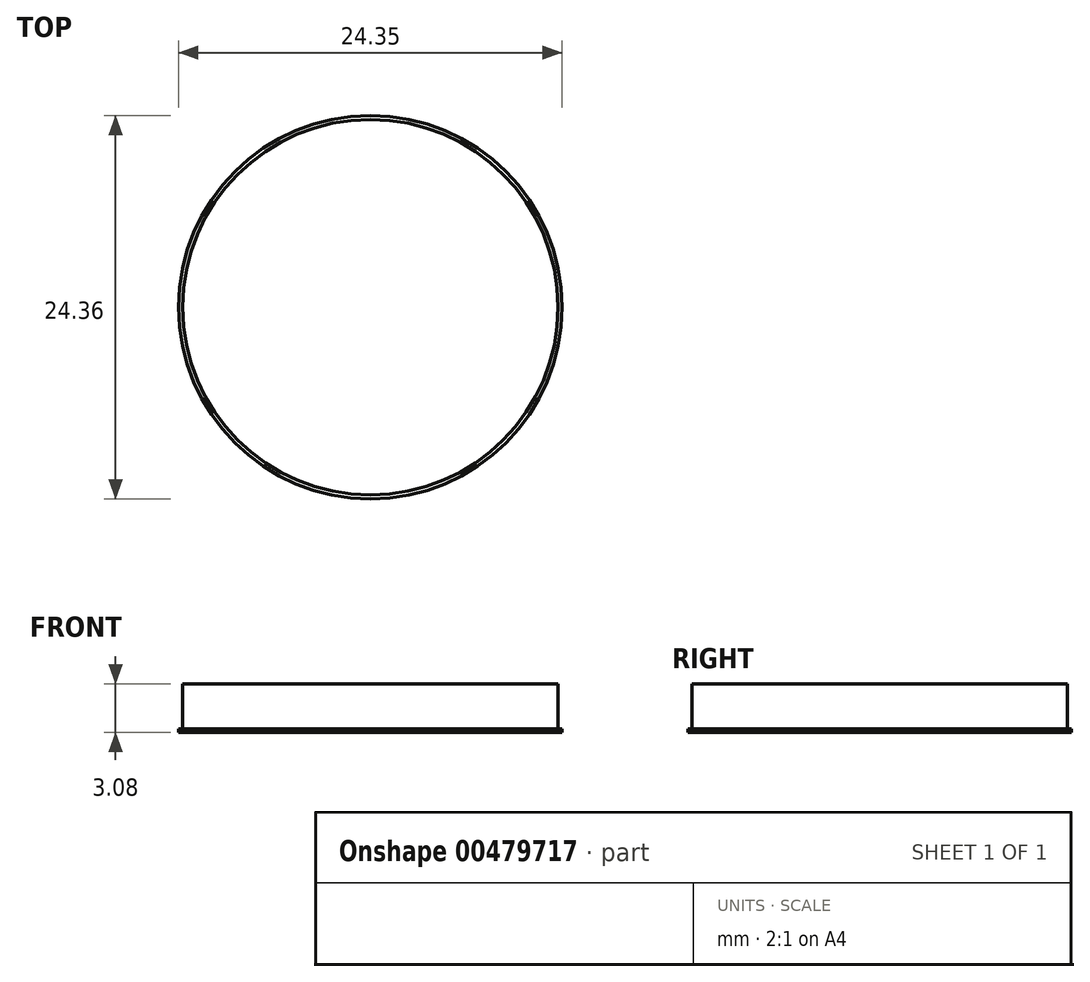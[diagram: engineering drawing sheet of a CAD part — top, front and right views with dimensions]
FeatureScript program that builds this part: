
annotation { "Feature Type Name" : "Feature", "Feature Type Description" : "" }
export const myFeature = defineFeature(function(context is Context, id is Id, definition is map)
    precondition{}
    {
        {
            var Q0;
            Q0=qCreatedBy(makeId("Front.planeOp"),FACE);
            var sketch = newSketch(context, id + "F0", { "sketchPlane" : qUnion([Q0])});
            skLineSegment(sketch, "E0", {"start": v(9.83, -1.87) * mm, "end": v(-5.17, -1.87) * mm});
            skLineSegment(sketch, "E1", {"start": v(-5.17, -1.87) * mm, "end": v(-5.17, 2.13) * mm});
            skLineSegment(sketch, "E2", {"start": v(-5.17, 2.13) * mm, "end": v(-2.17, 2.13) * mm});
            skLineSegment(sketch, "E3", {"start": v(-2.17, 2.13) * mm, "end": v(-2.17, 0.13) * mm});
            skLineSegment(sketch, "E4", {"start": v(-2.17, 0.13) * mm, "end": v(-2.47, 0.13) * mm});
            skLineSegment(sketch, "E5", {"start": v(-2.47, 0.13) * mm, "end": v(-2.47, -0.37) * mm});
            skLineSegment(sketch, "E6", {"start": v(-2.47, -0.37) * mm, "end": v(9.83, -0.37) * mm});
            skLineSegment(sketch, "E7", {"start": v(9.83, -0.37) * mm, "end": v(9.83, -1.87) * mm});
            skSolve(sketch);
        }
        {
            var Q0;
            Q0=makeQuery(id+"F0.imprint","IMPRINT",FACE,{"disambiguationData":[TD([[makeQuery(id+"F0.imprint","IMPRINT",EDGE,{"derivedFrom":sQuery(id+"F0.wireOp",EDGE,"E0")}),-1.0]])]});
            var sketch = newSketch(context, id + "F1", { "sketchPlane" : qUnion([Q0])});
            skLineSegment(sketch, "E8", {"start": v(9.83, -0.22) * mm, "end": v(-2.35, -0.22) * mm});
            skLineSegment(sketch, "E9", {"start": v(-2.35, -0.22) * mm, "end": v(-2.35, 0) * mm});
            skLineSegment(sketch, "E10", {"start": v(-2.35, 0) * mm, "end": v(-2.1, 0) * mm});
            skLineSegment(sketch, "E11", {"start": v(-2.1, 0) * mm, "end": v(-2.1, 2.36) * mm});
            skLineSegment(sketch, "E12", {"start": v(-2.1, 2.36) * mm, "end": v(9.83, 2.36) * mm});
            skLineSegment(sketch, "E13", {"start": v(9.83, 2.36) * mm, "end": v(9.83, -0.22) * mm});
            skLineSegment(sketch, "E14", {"start": v(-2.1, 2.36) * mm, "end": v(-2.1, 2.86) * mm});
            skLineSegment(sketch, "E15", {"start": v(-2.1, 2.86) * mm, "end": v(9.83, 2.86) * mm});
            skLineSegment(sketch, "E16", {"start": v(9.83, 2.86) * mm, "end": v(9.83, 2.36) * mm});
            skSolve(sketch);
        }
        {
            var Q0;
            Q0=makeQuery(id+"F1.imprint","IMPRINT",FACE,{"disambiguationData":[TD([[makeQuery(id+"F1.imprint","IMPRINT",EDGE,{"derivedFrom":sQuery(id+"F1.wireOp",EDGE,"E8")}),-1.0]])]});
            var Q1;
            Q1=makeQuery(id+"F1.imprint","IMPRINT",FACE,{"disambiguationData":[TD([[makeQuery(id+"F1.imprint","IMPRINT",EDGE,{"derivedFrom":sQuery(id+"F1.wireOp",EDGE,"E12")}),1.0]])]});
            var Q2;
            Q2=sQuery(id+"F1.wireOp",EDGE,"E13");
            revolve(context, id + "F2", {"entities" : qUnion([Q0, Q1]), "axis" : qUnion([Q2]), "revolveType" : RevolveType.FULL});
        }
    });
